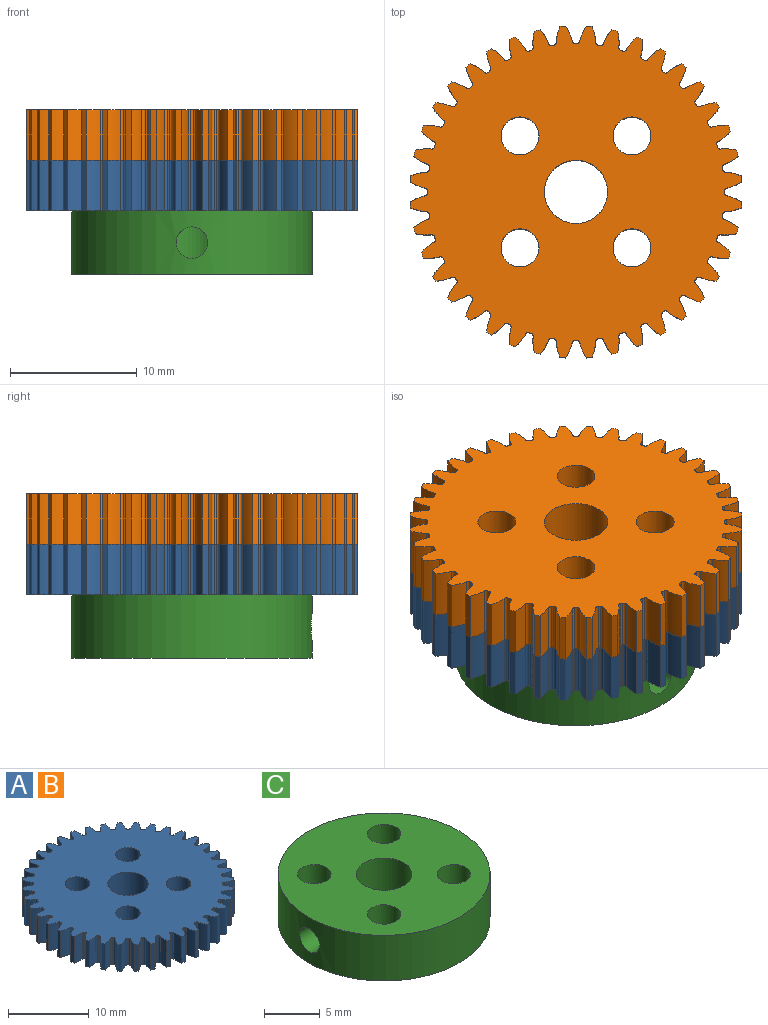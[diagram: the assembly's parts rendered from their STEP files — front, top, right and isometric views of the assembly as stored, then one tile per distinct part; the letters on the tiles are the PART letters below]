
ASSEMBLY  parts=3 mates=2
PART A: 247 faces, bbox 26.2x26.2x4 mm
  f0: cylinder r=13.12mm len=4mm, axis (0,0,-1), area 1.9mm2, adj f39,f42,f148,f240
  f1: cylinder r=13.12mm len=4mm, axis (0,0,-1), area 1.9mm2, adj f39,f42,f235,f238
  f2: cylinder r=13.12mm len=4mm, axis (0,0,-1), area 1.9mm2, adj f39,f42,f230,f233
  f3: cylinder r=13.12mm len=4mm, axis (0,0,-1), area 1.9mm2, adj f39,f42,f225,f228
  f4: cylinder r=13.12mm len=4mm, axis (0,0,-1), area 1.9mm2, adj f39,f42,f220,f223
  f5: cylinder r=13.12mm len=4mm, axis (0,0,-1), area 1.9mm2, adj f39,f42,f215,f218
  f6: cylinder r=13.12mm len=4mm, axis (0,0,-1), area 1.9mm2, adj f39,f42,f210,f213
  f7: cylinder r=13.12mm len=4mm, axis (0,0,-1), area 1.9mm2, adj f39,f42,f205,f208
  f8: cylinder r=13.12mm len=4mm, axis (0,0,-1), area 1.9mm2, adj f39,f42,f193,f200
  f9: cylinder r=13.12mm len=4mm, axis (0,0,-1), area 1.9mm2, adj f39,f42,f195,f203
  f10: cylinder r=13.12mm len=4mm, axis (0,0,-1), area 1.9mm2, adj f39,f42,f190,f198
  f11: cylinder r=13.12mm len=4mm, axis (0,0,-1), area 1.9mm2, adj f39,f42,f185,f188
  f12: cylinder r=13.12mm len=4mm, axis (0,0,-1), area 1.9mm2, adj f39,f42,f180,f183
  f13: cylinder r=13.12mm len=4mm, axis (0,0,-1), area 1.9mm2, adj f39,f42,f175,f178
  f14: cylinder r=13.12mm len=4mm, axis (0,0,-1), area 1.9mm2, adj f39,f42,f170,f173
  f15: cylinder r=13.12mm len=4mm, axis (0,0,-1), area 1.9mm2, adj f39,f42,f165,f168
  f16: cylinder r=13.12mm len=4mm, axis (0,0,-1), area 1.9mm2, adj f39,f42,f138,f160
  f17: cylinder r=13.12mm len=4mm, axis (0,0,-1), area 1.9mm2, adj f39,f42,f155,f158
  f18: cylinder r=13.12mm len=4mm, axis (0,0,-1), area 1.9mm2, adj f39,f42,f143,f150
  f19: cylinder r=13.12mm len=4mm, axis (0,0,-1), area 1.9mm2, adj f39,f42,f145,f153
  f20: cylinder r=13.12mm len=4mm, axis (0,0,-1), area 1.9mm2, adj f39,f42,f133,f140
  f21: cylinder r=13.12mm len=4mm, axis (0,0,-1), area 1.9mm2, adj f39,f42,f128,f135
  f22: cylinder r=13.12mm len=4mm, axis (0,0,-1), area 1.9mm2, adj f39,f42,f123,f130
  f23: cylinder r=13.12mm len=4mm, axis (0,0,-1), area 1.9mm2, adj f39,f42,f83,f125
  f24: cylinder r=13.12mm len=4mm, axis (0,0,-1), area 1.9mm2, adj f39,f42,f43,f120
  f25: cylinder r=13.12mm len=4mm, axis (0,0,-1), area 1.9mm2, adj f39,f42,f115,f118
  f26: cylinder r=13.12mm len=4mm, axis (0,0,-1), area 1.9mm2, adj f39,f42,f110,f113
  f27: cylinder r=13.12mm len=4mm, axis (0,0,-1), area 1.9mm2, adj f39,f42,f105,f108
  f28: cylinder r=13.12mm len=4mm, axis (0,0,-1), area 1.9mm2, adj f39,f42,f93,f100
  f29: cylinder r=13.12mm len=4mm, axis (0,0,-1), area 1.9mm2, adj f39,f42,f95,f103
  f30: cylinder r=13.12mm len=4mm, axis (0,0,-1), area 1.9mm2, adj f39,f42,f90,f98
  f31: cylinder r=13.12mm len=4mm, axis (0,0,-1), area 1.9mm2, adj f39,f42,f85,f88
  f32: cylinder r=13.12mm len=4mm, axis (0,0,-1), area 1.9mm2, adj f39,f42,f68,f80
  f33: cylinder r=13.12mm len=4mm, axis (0,0,-1), area 1.9mm2, adj f39,f42,f75,f78
  f34: cylinder r=13.12mm len=4mm, axis (0,0,-1), area 1.9mm2, adj f39,f42,f63,f70
  f35: cylinder r=13.12mm len=4mm, axis (0,0,-1), area 1.9mm2, adj f39,f42,f65,f163
  f36: cylinder r=13.12mm len=4mm, axis (0,0,-1), area 1.9mm2, adj f39,f42,f60,f73
  f37: cylinder r=13.12mm len=4mm, axis (0,0,-1), area 1.9mm2, adj f39,f42,f55,f58
  f38: cylinder r=13.12mm len=4mm, axis (0,0,-1), area 1.9mm2, adj f39,f42,f50,f53
  f39: plane 26.2x26.2mm, normal (0,0,1), area 439.3mm2, adj f0,f1,f2,f3,f4,f5,f6,f7
  f40: cylinder r=2.5mm len=5mm, axis (0,0,-1), area 62.8mm2, adj f39,f42
  f41: cylinder r=13.12mm len=4mm, axis (0,0,-1), area 1.9mm2, adj f39,f42,f45,f48
  f42: plane 26.2x26.2mm, normal (0,0,-1), area 439.3mm2, adj f0,f1,f2,f3,f4,f5,f6,f7
  f43: extruded ~4x1.2mm, area 5.2mm2, adj f24,f39,f42,f46
  f44: cylinder r=11.72mm len=4mm, axis (0,0,-1), area 0.7mm2, adj f39,f42,f46,f47
  f45: extruded ~4x1.2mm, area 5.2mm2, adj f39,f41,f42,f47
  f46: cylinder r=0.22mm len=4mm, axis (0,0,-1), area 1.2mm2, adj f39,f42,f43,f44
  f47: cylinder r=0.22mm len=4mm, axis (0,0,-1), area 1.2mm2, adj f39,f42,f44,f45
  f48: extruded ~4x1.26mm, area 5.2mm2, adj f39,f41,f42,f51
  f49: cylinder r=11.72mm len=4mm, axis (0,0,-1), area 0.7mm2, adj f39,f42,f51,f52
  f50: extruded ~4x1.11mm, area 5.2mm2, adj f38,f39,f42,f52
  f51: cylinder r=0.22mm len=4mm, axis (0,0,-1), area 1.2mm2, adj f39,f42,f48,f49
  f52: cylinder r=0.22mm len=4mm, axis (0,0,-1), area 1.2mm2, adj f39,f42,f49,f50
  f53: extruded ~4x1.29mm, area 5.2mm2, adj f38,f39,f42,f56
  f54: cylinder r=11.72mm len=4mm, axis (0,0,-1), area 0.7mm2, adj f39,f42,f56,f57
  f55: extruded ~4x0.99mm, area 5.2mm2, adj f37,f39,f42,f57
  f56: cylinder r=0.22mm len=4mm, axis (0,0,-1), area 1.2mm2, adj f39,f42,f53,f54
  f57: cylinder r=0.22mm len=4mm, axis (0,0,-1), area 1.2mm2, adj f39,f42,f54,f55
  f58: extruded ~4x1.29mm, area 5.2mm2, adj f37,f39,f42,f61
  f59: cylinder r=11.72mm len=4mm, axis (0,0,-1), area 0.7mm2, adj f39,f42,f61,f62
  f60: extruded ~4x0.98mm, area 5.2mm2, adj f36,f39,f42,f62
  f61: cylinder r=0.22mm len=4mm, axis (0,0,-1), area 1.2mm2, adj f39,f42,f58,f59
  f62: cylinder r=0.22mm len=4mm, axis (0,0,-1), area 1.2mm2, adj f39,f42,f59,f60
  f63: extruded ~4x0.98mm, area 5.2mm2, adj f34,f39,f42,f66
  f64: cylinder r=11.72mm len=4mm, axis (0,0,-1), area 0.7mm2, adj f39,f42,f66,f67
  f65: extruded ~4x1.29mm, area 5.2mm2, adj f35,f39,f42,f67
  f66: cylinder r=0.22mm len=4mm, axis (0,0,-1), area 1.2mm2, adj f39,f42,f63,f64
  f67: cylinder r=0.22mm len=4mm, axis (0,0,-1), area 1.2mm2, adj f39,f42,f64,f65
  f68: extruded ~4x1.1mm, area 5.2mm2, adj f32,f39,f42,f71
  f69: cylinder r=11.72mm len=4mm, axis (0,0,-1), area 0.7mm2, adj f39,f42,f71,f72
  f70: extruded ~4x1.26mm, area 5.2mm2, adj f34,f39,f42,f72
  f71: cylinder r=0.22mm len=4mm, axis (0,0,-1), area 1.2mm2, adj f39,f42,f68,f69
  f72: cylinder r=0.22mm len=4mm, axis (0,0,-1), area 1.2mm2, adj f39,f42,f69,f70
  f73: extruded ~4x1.26mm, area 5.2mm2, adj f36,f39,f42,f76
  f74: cylinder r=11.72mm len=4mm, axis (0,0,-1), area 0.7mm2, adj f39,f42,f76,f77
  f75: extruded ~4x1.1mm, area 5.2mm2, adj f33,f39,f42,f77
  f76: cylinder r=0.22mm len=4mm, axis (0,0,-1), area 1.2mm2, adj f39,f42,f73,f74
  f77: cylinder r=0.22mm len=4mm, axis (0,0,-1), area 1.2mm2, adj f39,f42,f74,f75
  f78: extruded ~4x1.19mm, area 5.2mm2, adj f33,f39,f42,f81
  f79: cylinder r=11.72mm len=4mm, axis (0,0,-1), area 0.7mm2, adj f39,f42,f81,f82
  f80: extruded ~4x1.19mm, area 5.2mm2, adj f32,f39,f42,f82
  f81: cylinder r=0.22mm len=4mm, axis (0,0,-1), area 1.2mm2, adj f39,f42,f78,f79
  f82: cylinder r=0.22mm len=4mm, axis (0,0,-1), area 1.2mm2, adj f39,f42,f79,f80
  f83: extruded ~4x1.29mm, area 5.2mm2, adj f23,f39,f42,f86
  f84: cylinder r=11.72mm len=4mm, axis (0,0,-1), area 0.7mm2, adj f39,f42,f86,f87
  f85: extruded ~4x0.99mm, area 5.2mm2, adj f31,f39,f42,f87
  f86: cylinder r=0.22mm len=4mm, axis (0,0,-1), area 1.2mm2, adj f39,f42,f83,f84
  f87: cylinder r=0.22mm len=4mm, axis (0,0,-1), area 1.2mm2, adj f39,f42,f84,f85
  f88: extruded ~4x1.29mm, area 5.2mm2, adj f31,f39,f42,f91
  f89: cylinder r=11.72mm len=4mm, axis (0,0,-1), area 0.7mm2, adj f39,f42,f91,f92
  f90: extruded ~4x0.98mm, area 5.2mm2, adj f30,f39,f42,f92
  f91: cylinder r=0.22mm len=4mm, axis (0,0,-1), area 1.2mm2, adj f39,f42,f88,f89
  f92: cylinder r=0.22mm len=4mm, axis (0,0,-1), area 1.2mm2, adj f39,f42,f89,f90
  f93: extruded ~4x1.19mm, area 5.2mm2, adj f28,f39,f42,f96
  f94: cylinder r=11.72mm len=4mm, axis (0,0,-1), area 0.7mm2, adj f39,f42,f96,f97
  f95: extruded ~4x1.19mm, area 5.2mm2, adj f29,f39,f42,f97
  f96: cylinder r=0.22mm len=4mm, axis (0,0,-1), area 1.2mm2, adj f39,f42,f93,f94
  f97: cylinder r=0.22mm len=4mm, axis (0,0,-1), area 1.2mm2, adj f39,f42,f94,f95
  f98: extruded ~4x1.26mm, area 5.2mm2, adj f30,f39,f42,f101
  f99: cylinder r=11.72mm len=4mm, axis (0,0,-1), area 0.7mm2, adj f39,f42,f101,f102
  f100: extruded ~4x1.1mm, area 5.2mm2, adj f28,f39,f42,f102
  f101: cylinder r=0.22mm len=4mm, axis (0,0,-1), area 1.2mm2, adj f39,f42,f98,f99
  f102: cylinder r=0.22mm len=4mm, axis (0,0,-1), area 1.2mm2, adj f39,f42,f99,f100
  f103: extruded ~4x1.1mm, area 5.2mm2, adj f29,f39,f42,f106
  f104: cylinder r=11.72mm len=4mm, axis (0,0,-1), area 0.7mm2, adj f39,f42,f106,f107
  f105: extruded ~4x1.26mm, area 5.2mm2, adj f27,f39,f42,f107
  f106: cylinder r=0.22mm len=4mm, axis (0,0,-1), area 1.2mm2, adj f39,f42,f103,f104
  f107: cylinder r=0.22mm len=4mm, axis (0,0,-1), area 1.2mm2, adj f39,f42,f104,f105
  f108: extruded ~4x0.98mm, area 5.2mm2, adj f27,f39,f42,f111
  f109: cylinder r=11.72mm len=4mm, axis (0,0,-1), area 0.7mm2, adj f39,f42,f111,f112
  f110: extruded ~4x1.29mm, area 5.2mm2, adj f26,f39,f42,f112
  f111: cylinder r=0.22mm len=4mm, axis (0,0,-1), area 1.2mm2, adj f39,f42,f108,f109
  f112: cylinder r=0.22mm len=4mm, axis (0,0,-1), area 1.2mm2, adj f39,f42,f109,f110
  f113: extruded ~4x0.99mm, area 5.2mm2, adj f26,f39,f42,f116
  f114: cylinder r=11.72mm len=4mm, axis (0,0,-1), area 0.7mm2, adj f39,f42,f116,f117
  f115: extruded ~4x1.29mm, area 5.2mm2, adj f25,f39,f42,f117
  f116: cylinder r=0.22mm len=4mm, axis (0,0,-1), area 1.2mm2, adj f39,f42,f113,f114
  f117: cylinder r=0.22mm len=4mm, axis (0,0,-1), area 1.2mm2, adj f39,f42,f114,f115
  f118: extruded ~4x1.11mm, area 5.2mm2, adj f25,f39,f42,f121
  f119: cylinder r=11.72mm len=4mm, axis (0,0,-1), area 0.7mm2, adj f39,f42,f121,f122
  f120: extruded ~4x1.26mm, area 5.2mm2, adj f24,f39,f42,f122
  f121: cylinder r=0.22mm len=4mm, axis (0,0,-1), area 1.2mm2, adj f39,f42,f118,f119
  f122: cylinder r=0.22mm len=4mm, axis (0,0,-1), area 1.2mm2, adj f39,f42,f119,f120
  f123: extruded ~4x1.26mm, area 5.2mm2, adj f22,f39,f42,f126
  f124: cylinder r=11.72mm len=4mm, axis (0,0,-1), area 0.7mm2, adj f39,f42,f126,f127
  f125: extruded ~4x1.11mm, area 5.2mm2, adj f23,f39,f42,f127
  f126: cylinder r=0.22mm len=4mm, axis (0,0,-1), area 1.2mm2, adj f39,f42,f123,f124
  f127: cylinder r=0.22mm len=4mm, axis (0,0,-1), area 1.2mm2, adj f39,f42,f124,f125
  f128: extruded ~4x1.2mm, area 5.2mm2, adj f21,f39,f42,f131
  f129: cylinder r=11.72mm len=4mm, axis (0,0,-1), area 0.7mm2, adj f39,f42,f131,f132
  f130: extruded ~4x1.2mm, area 5.2mm2, adj f22,f39,f42,f132
  f131: cylinder r=0.22mm len=4mm, axis (0,0,-1), area 1.2mm2, adj f39,f42,f128,f129
  f132: cylinder r=0.22mm len=4mm, axis (0,0,-1), area 1.2mm2, adj f39,f42,f129,f130
  f133: extruded ~4x1.11mm, area 5.2mm2, adj f20,f39,f42,f136
  f134: cylinder r=11.72mm len=4mm, axis (0,0,-1), area 0.7mm2, adj f39,f42,f136,f137
  f135: extruded ~4x1.26mm, area 5.2mm2, adj f21,f39,f42,f137
  f136: cylinder r=0.22mm len=4mm, axis (0,0,-1), area 1.2mm2, adj f39,f42,f133,f134
  f137: cylinder r=0.22mm len=4mm, axis (0,0,-1), area 1.2mm2, adj f39,f42,f134,f135
  f138: extruded ~4x0.99mm, area 5.2mm2, adj f16,f39,f42,f141
  f139: cylinder r=11.72mm len=4mm, axis (0,0,-1), area 0.7mm2, adj f39,f42,f141,f142
  f140: extruded ~4x1.29mm, area 5.2mm2, adj f20,f39,f42,f142
  f141: cylinder r=0.22mm len=4mm, axis (0,0,-1), area 1.2mm2, adj f39,f42,f138,f139
  f142: cylinder r=0.22mm len=4mm, axis (0,0,-1), area 1.2mm2, adj f39,f42,f139,f140
  f143: extruded ~4x1.19mm, area 5.2mm2, adj f18,f39,f42,f146
  f144: cylinder r=11.72mm len=4mm, axis (0,0,-1), area 0.7mm2, adj f39,f42,f146,f147
  f145: extruded ~4x1.19mm, area 5.2mm2, adj f19,f39,f42,f147
  f146: cylinder r=0.22mm len=4mm, axis (0,0,-1), area 1.2mm2, adj f39,f42,f143,f144
  f147: cylinder r=0.22mm len=4mm, axis (0,0,-1), area 1.2mm2, adj f39,f42,f144,f145
  f148: extruded ~4x1.26mm, area 5.2mm2, adj f0,f39,f42,f151
  f149: cylinder r=11.72mm len=4mm, axis (0,0,-1), area 0.7mm2, adj f39,f42,f151,f152
  f150: extruded ~4x1.1mm, area 5.2mm2, adj f18,f39,f42,f152
  f151: cylinder r=0.22mm len=4mm, axis (0,0,-1), area 1.2mm2, adj f39,f42,f148,f149
  f152: cylinder r=0.22mm len=4mm, axis (0,0,-1), area 1.2mm2, adj f39,f42,f149,f150
  f153: extruded ~4x1.1mm, area 5.2mm2, adj f19,f39,f42,f156
  f154: cylinder r=11.72mm len=4mm, axis (0,0,-1), area 0.7mm2, adj f39,f42,f156,f157
  f155: extruded ~4x1.26mm, area 5.2mm2, adj f17,f39,f42,f157
  f156: cylinder r=0.22mm len=4mm, axis (0,0,-1), area 1.2mm2, adj f39,f42,f153,f154
  f157: cylinder r=0.22mm len=4mm, axis (0,0,-1), area 1.2mm2, adj f39,f42,f154,f155
  f158: extruded ~4x0.98mm, area 5.2mm2, adj f17,f39,f42,f161
  f159: cylinder r=11.72mm len=4mm, axis (0,0,-1), area 0.7mm2, adj f39,f42,f161,f162
  f160: extruded ~4x1.29mm, area 5.2mm2, adj f16,f39,f42,f162
  f161: cylinder r=0.22mm len=4mm, axis (0,0,-1), area 1.2mm2, adj f39,f42,f158,f159
  f162: cylinder r=0.22mm len=4mm, axis (0,0,-1), area 1.2mm2, adj f39,f42,f159,f160
  f163: extruded ~4x0.99mm, area 5.2mm2, adj f35,f39,f42,f166
  f164: cylinder r=11.72mm len=4mm, axis (0,0,-1), area 0.7mm2, adj f39,f42,f166,f167
  f165: extruded ~4x1.29mm, area 5.2mm2, adj f15,f39,f42,f167
  f166: cylinder r=0.22mm len=4mm, axis (0,0,-1), area 1.2mm2, adj f39,f42,f163,f164
  f167: cylinder r=0.22mm len=4mm, axis (0,0,-1), area 1.2mm2, adj f39,f42,f164,f165
  f168: extruded ~4x1.11mm, area 5.2mm2, adj f15,f39,f42,f171
  f169: cylinder r=11.72mm len=4mm, axis (0,0,-1), area 0.7mm2, adj f39,f42,f171,f172
  f170: extruded ~4x1.26mm, area 5.2mm2, adj f14,f39,f42,f172
  f171: cylinder r=0.22mm len=4mm, axis (0,0,-1), area 1.2mm2, adj f39,f42,f168,f169
  f172: cylinder r=0.22mm len=4mm, axis (0,0,-1), area 1.2mm2, adj f39,f42,f169,f170
  f173: extruded ~4x1.2mm, area 5.2mm2, adj f14,f39,f42,f176
  f174: cylinder r=11.72mm len=4mm, axis (0,0,-1), area 0.7mm2, adj f39,f42,f176,f177
  f175: extruded ~4x1.2mm, area 5.2mm2, adj f13,f39,f42,f177
  f176: cylinder r=0.22mm len=4mm, axis (0,0,-1), area 1.2mm2, adj f39,f42,f173,f174
  f177: cylinder r=0.22mm len=4mm, axis (0,0,-1), area 1.2mm2, adj f39,f42,f174,f175
  f178: extruded ~4x1.26mm, area 5.2mm2, adj f13,f39,f42,f181
  f179: cylinder r=11.72mm len=4mm, axis (0,0,-1), area 0.7mm2, adj f39,f42,f181,f182
  f180: extruded ~4x1.11mm, area 5.2mm2, adj f12,f39,f42,f182
  f181: cylinder r=0.22mm len=4mm, axis (0,0,-1), area 1.2mm2, adj f39,f42,f178,f179
  f182: cylinder r=0.22mm len=4mm, axis (0,0,-1), area 1.2mm2, adj f39,f42,f179,f180
  f183: extruded ~4x1.29mm, area 5.2mm2, adj f12,f39,f42,f186
  f184: cylinder r=11.72mm len=4mm, axis (0,0,-1), area 0.7mm2, adj f39,f42,f186,f187
  f185: extruded ~4x0.99mm, area 5.2mm2, adj f11,f39,f42,f187
  f186: cylinder r=0.22mm len=4mm, axis (0,0,-1), area 1.2mm2, adj f39,f42,f183,f184
  f187: cylinder r=0.22mm len=4mm, axis (0,0,-1), area 1.2mm2, adj f39,f42,f184,f185
  f188: extruded ~4x1.29mm, area 5.2mm2, adj f11,f39,f42,f191
  f189: cylinder r=11.72mm len=4mm, axis (0,0,-1), area 0.7mm2, adj f39,f42,f191,f192
  f190: extruded ~4x0.98mm, area 5.2mm2, adj f10,f39,f42,f192
  f191: cylinder r=0.22mm len=4mm, axis (0,0,-1), area 1.2mm2, adj f39,f42,f188,f189
  f192: cylinder r=0.22mm len=4mm, axis (0,0,-1), area 1.2mm2, adj f39,f42,f189,f190
  f193: extruded ~4x1.19mm, area 5.2mm2, adj f8,f39,f42,f196
  f194: cylinder r=11.72mm len=4mm, axis (0,0,-1), area 0.7mm2, adj f39,f42,f196,f197
  f195: extruded ~4x1.19mm, area 5.2mm2, adj f9,f39,f42,f197
  f196: cylinder r=0.22mm len=4mm, axis (0,0,-1), area 1.2mm2, adj f39,f42,f193,f194
  f197: cylinder r=0.22mm len=4mm, axis (0,0,-1), area 1.2mm2, adj f39,f42,f194,f195
  f198: extruded ~4x1.26mm, area 5.2mm2, adj f10,f39,f42,f201
  f199: cylinder r=11.72mm len=4mm, axis (0,0,-1), area 0.7mm2, adj f39,f42,f201,f202
  f200: extruded ~4x1.1mm, area 5.2mm2, adj f8,f39,f42,f202
  f201: cylinder r=0.22mm len=4mm, axis (0,0,-1), area 1.2mm2, adj f39,f42,f198,f199
  f202: cylinder r=0.22mm len=4mm, axis (0,0,-1), area 1.2mm2, adj f39,f42,f199,f200
  f203: extruded ~4x1.1mm, area 5.2mm2, adj f9,f39,f42,f206
  f204: cylinder r=11.72mm len=4mm, axis (0,0,-1), area 0.7mm2, adj f39,f42,f206,f207
  f205: extruded ~4x1.26mm, area 5.2mm2, adj f7,f39,f42,f207
  f206: cylinder r=0.22mm len=4mm, axis (0,0,-1), area 1.2mm2, adj f39,f42,f203,f204
  f207: cylinder r=0.22mm len=4mm, axis (0,0,-1), area 1.2mm2, adj f39,f42,f204,f205
  f208: extruded ~4x0.98mm, area 5.2mm2, adj f7,f39,f42,f211
  f209: cylinder r=11.72mm len=4mm, axis (0,0,-1), area 0.7mm2, adj f39,f42,f211,f212
  f210: extruded ~4x1.29mm, area 5.2mm2, adj f6,f39,f42,f212
  f211: cylinder r=0.22mm len=4mm, axis (0,0,-1), area 1.2mm2, adj f39,f42,f208,f209
  f212: cylinder r=0.22mm len=4mm, axis (0,0,-1), area 1.2mm2, adj f39,f42,f209,f210
  f213: extruded ~4x0.99mm, area 5.2mm2, adj f6,f39,f42,f216
  f214: cylinder r=11.72mm len=4mm, axis (0,0,-1), area 0.7mm2, adj f39,f42,f216,f217
  f215: extruded ~4x1.29mm, area 5.2mm2, adj f5,f39,f42,f217
  f216: cylinder r=0.22mm len=4mm, axis (0,0,-1), area 1.2mm2, adj f39,f42,f213,f214
  f217: cylinder r=0.22mm len=4mm, axis (0,0,-1), area 1.2mm2, adj f39,f42,f214,f215
  f218: extruded ~4x1.11mm, area 5.2mm2, adj f5,f39,f42,f221
  f219: cylinder r=11.72mm len=4mm, axis (0,0,-1), area 0.7mm2, adj f39,f42,f221,f222
  f220: extruded ~4x1.26mm, area 5.2mm2, adj f4,f39,f42,f222
  f221: cylinder r=0.22mm len=4mm, axis (0,0,-1), area 1.2mm2, adj f39,f42,f218,f219
  f222: cylinder r=0.22mm len=4mm, axis (0,0,-1), area 1.2mm2, adj f39,f42,f219,f220
  f223: extruded ~4x1.2mm, area 5.2mm2, adj f4,f39,f42,f226
  f224: cylinder r=11.72mm len=4mm, axis (0,0,-1), area 0.7mm2, adj f39,f42,f226,f227
  f225: extruded ~4x1.2mm, area 5.2mm2, adj f3,f39,f42,f227
  f226: cylinder r=0.22mm len=4mm, axis (0,0,-1), area 1.2mm2, adj f39,f42,f223,f224
  f227: cylinder r=0.22mm len=4mm, axis (0,0,-1), area 1.2mm2, adj f39,f42,f224,f225
  f228: extruded ~4x1.26mm, area 5.2mm2, adj f3,f39,f42,f231
  f229: cylinder r=11.72mm len=4mm, axis (0,0,-1), area 0.7mm2, adj f39,f42,f231,f232
  f230: extruded ~4x1.11mm, area 5.2mm2, adj f2,f39,f42,f232
  f231: cylinder r=0.22mm len=4mm, axis (0,0,-1), area 1.2mm2, adj f39,f42,f228,f229
  f232: cylinder r=0.22mm len=4mm, axis (0,0,-1), area 1.2mm2, adj f39,f42,f229,f230
  f233: extruded ~4x1.29mm, area 5.2mm2, adj f2,f39,f42,f236
  f234: cylinder r=11.72mm len=4mm, axis (0,0,-1), area 0.7mm2, adj f39,f42,f236,f237
  f235: extruded ~4x0.99mm, area 5.2mm2, adj f1,f39,f42,f237
  f236: cylinder r=0.22mm len=4mm, axis (0,0,-1), area 1.2mm2, adj f39,f42,f233,f234
  f237: cylinder r=0.22mm len=4mm, axis (0,0,-1), area 1.2mm2, adj f39,f42,f234,f235
  f238: extruded ~4x1.29mm, area 5.2mm2, adj f1,f39,f42,f241
  f239: cylinder r=11.72mm len=4mm, axis (0,0,-1), area 0.7mm2, adj f39,f42,f241,f242
  f240: extruded ~4x0.98mm, area 5.2mm2, adj f0,f39,f42,f242
  f241: cylinder r=0.22mm len=4mm, axis (0,0,-1), area 1.2mm2, adj f39,f42,f238,f239
  f242: cylinder r=0.22mm len=4mm, axis (0,0,-1), area 1.2mm2, adj f39,f42,f239,f240
  f243: cylinder r=1.5mm len=4mm, axis (0,0,1), area 37.7mm2, adj f39,f42
  f244: cylinder r=1.5mm len=4mm, axis (0,0,1), area 37.7mm2, adj f39,f42
  f245: cylinder r=1.5mm len=4mm, axis (0,0,1), area 37.7mm2, adj f39,f42
  f246: cylinder r=1.5mm len=4mm, axis (0,0,1), area 37.7mm2, adj f39,f42
PART B: same geometry as A
PART C: 9 faces, bbox 19x19x5 mm
  f0: cylinder r=2.5mm len=5mm, axis (0,0,-1), area 73.5mm2, adj f6,f7,f8
  f1: cylinder r=1.5mm len=5mm, axis (0,0,-1), area 47.1mm2, adj f6,f7
  f2: cylinder r=1.5mm len=5mm, axis (0,0,-1), area 47.1mm2, adj f6,f7
  f3: cylinder r=1.5mm len=5mm, axis (0,0,-1), area 47.1mm2, adj f6,f7
  f4: cylinder r=1.5mm len=5mm, axis (0,0,-1), area 47.1mm2, adj f6,f7
  f5: cylinder r=9.5mm len=19mm, axis (0,0,-1), area 293.6mm2, adj f6,f7,f8
  f6: plane 19x19mm, normal (0,0,1), area 235.6mm2, adj f0,f1,f2,f3,f4,f5
  f7: plane 19x19mm, normal (0,0,-1), area 235.6mm2, adj f0,f1,f2,f3,f4,f5
  f8: cylinder r=1.25mm len=7.34mm, axis (1,0,0), area 55.9mm2, adj f0,f5
PLACE A t=(-2.74,-1.3,-1.52)mm
PLACE B t=(-2.74,-1.3,2.48)mm
PLACE C rot(axis=(0.71,0.71,0),180deg) t=(-2.74,-1.3,-4.02)mm
MATE fastened B.f245 <-> A.f245  axis (0,0,-1) through (1.67,-5.72,2.48)mm
MATE fastened C.f3 <-> A.f246  axis (0,0,1) through (-7.16,-5.72,-1.52)mm
